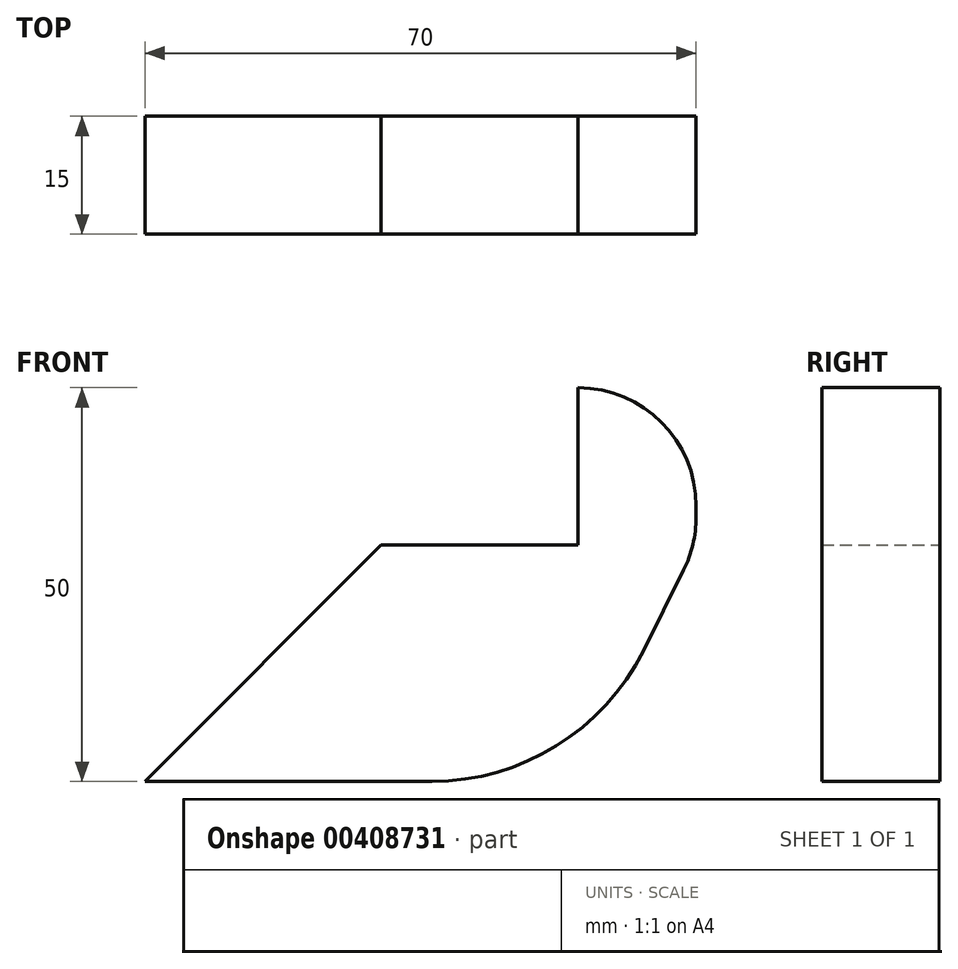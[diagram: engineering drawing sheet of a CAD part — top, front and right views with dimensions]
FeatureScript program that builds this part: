
annotation { "Feature Type Name" : "Feature", "Feature Type Description" : "" }
export const myFeature = defineFeature(function(context is Context, id is Id, definition is map)
    precondition{}
    {
        {
            assignVariable(context, id + "F0", {"name" : "noseProtrusion", "anyValue" : 15});
        }
        {
            assignVariable(context, id + "F1", {"name" : "width", "anyValue" : 15});
        }
        {
            assignVariable(context, id + "F2", {"name" : "bottomHeight", "anyValue" : 30});
        }
        {
            var Q0;
            Q0=qCreatedBy(makeId("Front.planeOp"),FACE);
            var sketch = newSketch(context, id + "F3", { "sketchPlane" : qUnion([Q0])});
            skLineSegment(sketch, "E0", {"start": v(0, 20) * mm, "end": v(0, 0) * mm});
            skLineSegment(sketch, "E1", {"start": v(0, 0) * mm, "end": v(-55, 0) * mm});
            skLineSegment(sketch, "E2", {"start": v(0, 10) * mm, "end": v(119.22, 10) * mm, "construction": true});
            skLineSegment(sketch, "E3", {"start": v(-55, 0) * mm, "end": v(-55, -30) * mm});
            skLineSegment(sketch, "E4", {"start": v(-55, -30) * mm, "end": v(0, -30) * mm});
            skLineSegment(sketch, "E5", {"start": v(0, -30) * mm, "end": v(15, 0) * mm});
            skLineSegment(sketch, "E6", {"start": v(15, 0) * mm, "end": v(15, 20) * mm});
            skLineSegment(sketch, "E7", {"start": v(15, 20) * mm, "end": v(0, 20) * mm});
            skLineSegment(sketch, "E8", {"start": v(0, 0) * mm, "end": v(0, -30) * mm});
            skLineSegment(sketch, "E9", {"start": v(0, 0) * mm, "end": v(15, 0) * mm});
            skSolve(sketch);
        }
        {
            var Q0;
            Q0 = qSketchRegion(id + "F3", true);
            extrude(context, id + "F4", {"entities" : qUnion([Q0]), "depth" : (getVariable(context, 'width')) * mm, "offsetDistance" : 25 * mm});
        }
        {
            var Q0;
            Q0=makeQuery(id+"F4.opExtrude","SWEPT_EDGE",EDGE,{"disambiguationData":[OSD([sQuery(id+"F3.wireOp",EDGE,"E5"),sQuery(id+"F3.wireOp",EDGE,"E6"),sQuery(id+"F3.wireOp",EDGE,"E9")])]});
            fillet(context, id + "F5", {"entities" : qUnion([Q0]), "radius" : (getVariable(context, 'noseProtrusion')) * mm, "tangentPropagation" : true, "allowEdgeOverflow" : false});
        }
        {
            var Q0;
            Q0=makeQuery(id+"F4.opExtrude","SWEPT_EDGE",EDGE,{"disambiguationData":[OSD([sQuery(id+"F3.wireOp",EDGE,"E4"),sQuery(id+"F3.wireOp",EDGE,"E5"),sQuery(id+"F3.wireOp",EDGE,"E8")])]});
            fillet(context, id + "F6", {"entities" : qUnion([Q0]), "radius" : (getVariable(context, 'bottomHeight')) * mm, "tangentPropagation" : true, "allowEdgeOverflow" : false});
        }
        {
            var Q0;
            Q0=makeQuery(id+"F4.opExtrude","SWEPT_EDGE",EDGE,{"disambiguationData":[OSD([sQuery(id+"F3.wireOp",EDGE,"E6"),sQuery(id+"F3.wireOp",EDGE,"E7")])]});
            fillet(context, id + "F7", {"entities" : qUnion([Q0]), "radius" : (getVariable(context, 'noseProtrusion')) * mm, "tangentPropagation" : true, "allowEdgeOverflow" : false});
        }
        {
            var Q0;
            Q0=makeQuery(id+"F4.opExtrude","CAP_FACE",FACE,{"disambiguationData":[OSD([sQuery(id+"F3.wireOp",EDGE,"E0"),sQuery(id+"F3.wireOp",EDGE,"E1"),sQuery(id+"F3.wireOp",EDGE,"E3"),sQuery(id+"F3.wireOp",EDGE,"E4"),sQuery(id+"F3.wireOp",EDGE,"E5"),sQuery(id+"F3.wireOp",EDGE,"E6"),sQuery(id+"F3.wireOp",EDGE,"E7")])],"isStart":true});
            var sketch = newSketch(context, id + "F8", { "sketchPlane" : qUnion([Q0])});
            skLineSegment(sketch, "E10", {"start": v(55, -30) * mm, "end": v(25, 0) * mm});
            skLineSegment(sketch, "E11", {"start": v(25, 0) * mm, "end": v(55, 0) * mm});
            skLineSegment(sketch, "E12", {"start": v(55, 0) * mm, "end": v(55, -30) * mm});
            skSolve(sketch);
        }
        {
            var Q0;
            Q0 = qSketchRegion(id + "F8", true);
            extrude(context, id + "F9", {"entities" : qUnion([Q0]), "operationType" : NewBodyOperationType.REMOVE, "endBound" : BoundingType.THROUGH_ALL, "oppositeDirection" : true, "depth" : 25 * mm, "offsetDistance" : 25 * mm});
        }
    });
